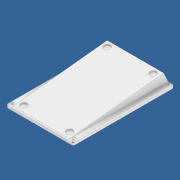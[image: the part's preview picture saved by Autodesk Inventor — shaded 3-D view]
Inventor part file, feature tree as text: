
AUTODESK INVENTOR PART (.ipt)
format: ipt  version: 2020 (Build 240168000, 168)  size: 356,352 bytes
history: native  units: in
note: dims shown in document units (in); Inventor stores cm internally (conversion verified against a paired STEP export)
features: extrude x12, sketch x12, fillet x4, plane x2
ambient origin geometry x8: Origin, YZ Plane, XZ Plane, XY Plane, X Axis, Y Axis, Z Axis, Center Point
bodies: Solid1 (feature_tree)
feature tree (30):
  extrude  "Extrusion1"  Depth=3.7795in
  fillet  "Fillet1"  Radius=0.1181in
  extrude  "Extrusion2"  Depth=0.0787in
  extrude  "Extrusion4"  Depth=0.0787in
  extrude  "Extrusion5"  Depth=0.1063in
  extrude  "Extrusion8"  Depth=0.1063in
  extrude  "Extrusion17"  Depth=0.1063in
  extrude  "Extrusion19"  Depth=0.1063in
  extrude  "Extrusion21"  Depth=0.3937in TaperAngle=0.0deg
  extrude  "Extrusion24"  Depth=0.1772in
  plane  "Work Plane4"
  extrude  "Extrusion25"  Depth=3.7402in
  plane  "Work Plane5"
  extrude  "Extrusion27"  Depth=1.1956in
  fillet  "Fillet5"  Radius=2.1181in
  fillet  "Fillet7"  Radius=0.2402in
  extrude  "Extrusion28"  Depth=0.0394in
  sketch  "Sketch35"  dims[d62=0.2402in d63=0.2402in d64=0.2402in d65=0.1969in d66=0.1969in d67=0.1969in d68=0.1969in d69=0.1969in d70=0.1969in d71=0.1969in d72=0.1969in d73=0.0394in d74=0.0in d106=0.748in d107=1.3386in d108=0.0788in d109=0.6654in d110=0.7087in d111=0.0in d116=0.1354in d117=0.748in d118=0.0in d122=0.0394in d123=0.0in d137=0.1575in d138=0.1575in d139=0.1575in d141=0.1575in d142=0.0118in d143=0.0in d144=0.3937in d145=0.1575in d146=0.1969in d147=0.7874in d148=0.0in d157=0.6299in d158=0.3346in d159=0.7441in d160=0.1311in d161=0.3937in d162=0.0in d163=0.0787in d166=0.1669in d167=0.1181in d168=0.1181in d169=0.0394in d170=0.0in d174=0.0394in]
  fillet  "Fillet8"  Radius=0.2402in
  sketch  "Sketch1"  dims[d0=2.5118in d1=3.7795in d2=0.1181in d3=0.0in]
  sketch  "Sketch2"  dims[d4=0.0591in d5=0.0787in]
  sketch  "Sketch4"  dims[d6=0.0787in d7=0.0787in]
  sketch  "Sketch5"  dims[d8=0.0787in d9=0.1063in]
  sketch  "Sketch9"  dims[d10=0.1063in d11=0.1063in]
  sketch  "Sketch20"  dims[d12=0.1063in d13=0.1063in]
  sketch  "Sketch22"  dims[d14=0.1063in d15=0.1063in]
  sketch  "Sketch29"  dims[d16=0.1063in d17=0.3937in d18=0.0in]
  sketch  "Sketch31"  dims[d37=2.1181in d38=0.1772in]
  sketch  "Sketch33"  dims[d39=3.7402in d40=3.7402in]
  sketch  "Sketch34"  dims[d41=0.3752in d42=0.0in d44=1.1956in d45=2.1181in d46=0.0in d61=0.2402in]
